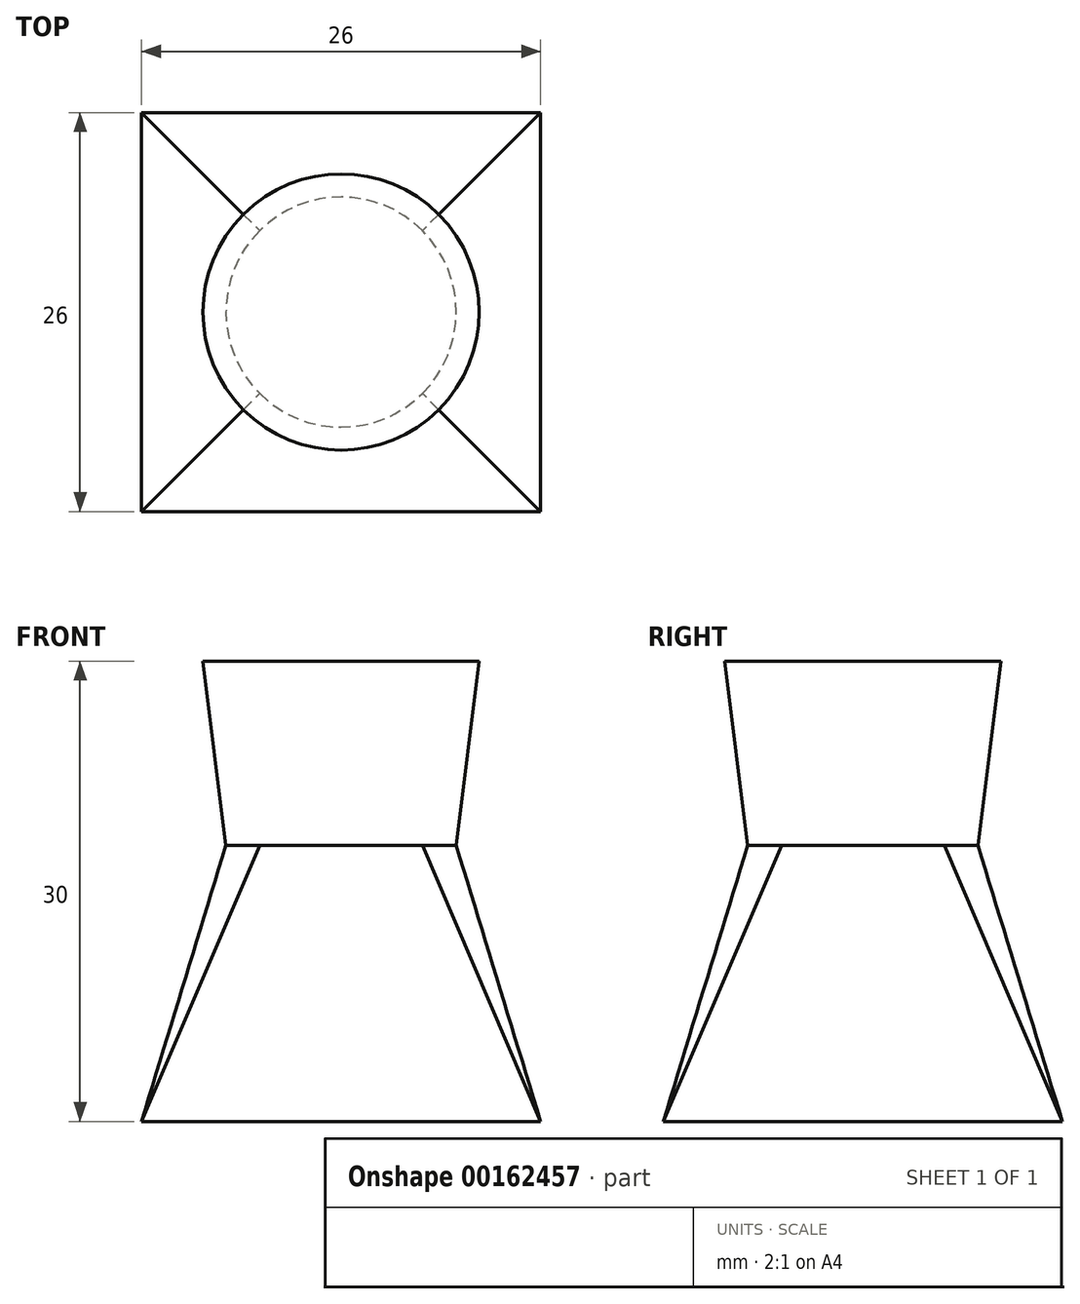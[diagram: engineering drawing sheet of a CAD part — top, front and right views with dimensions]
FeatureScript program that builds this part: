
annotation { "Feature Type Name" : "Feature", "Feature Type Description" : "" }
export const myFeature = defineFeature(function(context is Context, id is Id, definition is map)
    precondition{}
    {
        {
            var Q0;
            Q0=qCreatedBy(makeId("Top.planeOp"),FACE);
            var sketch = newSketch(context, id + "F0", { "sketchPlane" : qUnion([Q0])});
            skLineSegment(sketch, "E0.bottom", {"start": v(13, 13) * mm, "end": v(-13, 13) * mm});
            skLineSegment(sketch, "E0.top", {"start": v(13, -13) * mm, "end": v(-13, -13) * mm});
            skLineSegment(sketch, "E0.left", {"start": v(13, 13) * mm, "end": v(13, -13) * mm});
            skLineSegment(sketch, "E0.right", {"start": v(-13, 13) * mm, "end": v(-13, -13) * mm});
            skPoint(sketch, "E0.middle", {"position": v(0, 0) * mm});
            skSolve(sketch);
        }
        {
            var Q0;
            Q0=qCreatedBy(makeId("Top.planeOp"),FACE);
            cPlane(context, id + "F1", {"entities" : qUnion([Q0]), "cplaneType" : CPlaneType.OFFSET, "offset" : 18 * mm, "width" : 150 * mm, "height" : 150 * mm});
        }
        {
            var Q0;
            Q0=qCreatedBy(id+"F1.planeOp",FACE);
            cPlane(context, id + "F2", {"entities" : qUnion([Q0]), "cplaneType" : CPlaneType.OFFSET, "offset" : 12 * mm, "width" : 150 * mm, "height" : 150 * mm});
        }
        {
            var Q0;
            Q0=qCreatedBy(id+"F1.planeOp",FACE);
            var sketch = newSketch(context, id + "F3", { "sketchPlane" : qUnion([Q0])});
            skCircle(sketch, "E1", {"center": v(0, 0) * mm, "radius": 7.5 * mm});
            skSolve(sketch);
        }
        {
            var Q0;
            Q0=qCreatedBy(id+"F2.planeOp",FACE);
            var sketch = newSketch(context, id + "F4", { "sketchPlane" : qUnion([Q0])});
            skCircle(sketch, "E2", {"center": v(0, 0) * mm, "radius": 9 * mm});
            skSolve(sketch);
        }
        {
            var Q0;
            Q0=makeQuery(id+"F0.imprint","IMPRINT",FACE,{"disambiguationData":[TD([[makeQuery(id+"F0.imprint","IMPRINT",EDGE,{"derivedFrom":sQuery(id+"F0.wireOp",EDGE,"E0.bottom")}),1.0]])]});
            var Q1;
            Q1=makeQuery(id+"F3.imprint","IMPRINT",FACE,{"disambiguationData":[TD([[makeQuery(id+"F3.imprint","IMPRINT",EDGE,{"derivedFrom":sQuery(id+"F3.wireOp",EDGE,"E1")}),1.0]])]});
            loft(context, id + "F5", {"sheetProfilesArray" : [{ "sheetProfileEntities" : qUnion([Q0]) }, { "sheetProfileEntities" : qUnion([Q1]) }]});
        }
        {
            var Q1;
            Q1=makeQuery(id+"F5.opLoft","CAP_FACE",FACE,{"disambiguationData":[OSD([makeQuery(id+"F3.imprint","IMPRINT",FACE,{"disambiguationData":[TD([[makeQuery(id+"F3.imprint","IMPRINT",EDGE,{"derivedFrom":sQuery(id+"F3.wireOp",EDGE,"E1")}),1.0]])]})])],"isStart":true});
            var Q2;
            Q2=makeQuery(id+"F4.imprint","IMPRINT",FACE,{"disambiguationData":[TD([[makeQuery(id+"F4.imprint","IMPRINT",EDGE,{"derivedFrom":sQuery(id+"F4.wireOp",EDGE,"E2")}),1.0]])]});
            loft(context, id + "F6", {"operationType" : NewBodyOperationType.ADD, "sheetProfilesArray" : [{ "sheetProfileEntities" : qUnion([Q1]) }, { "sheetProfileEntities" : qUnion([Q2]) }]});
        }
    });
